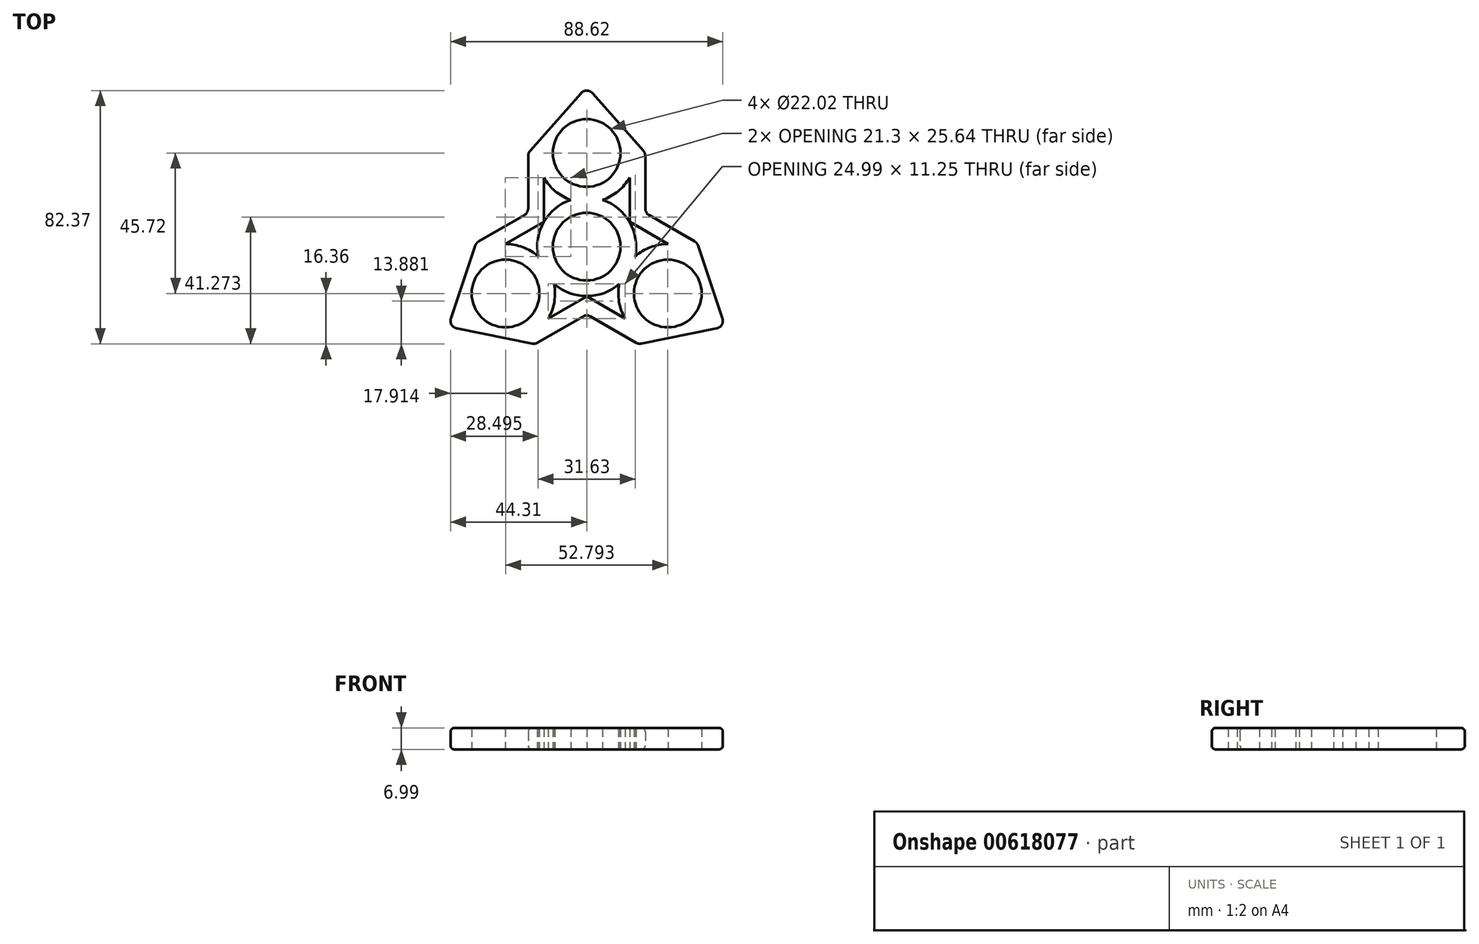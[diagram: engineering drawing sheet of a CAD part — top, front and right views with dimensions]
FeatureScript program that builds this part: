
annotation { "Feature Type Name" : "Feature", "Feature Type Description" : "" }
export const myFeature = defineFeature(function(context is Context, id is Id, definition is map)
    precondition{}
    {
        {
            var Q0;
            Q0=qCreatedBy(makeId("Top.planeOp"),FACE);
            var sketch = newSketch(context, id + "F0", { "sketchPlane" : qUnion([Q0])});
            skCircle(sketch, "E0", {"center": v(0, 0) * mm, "radius": 19.05 * mm});
            skLineSegment(sketch, "E1", {"start": v(0, 0) * mm, "end": v(0, 30.48) * mm});
            skCircle(sketch, "E2", {"center": v(0, 0) * mm, "radius": 11.01 * mm});
            skCircle(sketch, "E3", {"center": v(0, 30.48) * mm, "radius": 11.01 * mm});
            skLineSegment(sketch, "E4", {"start": v(-19.05, 30.48) * mm, "end": v(19.05, 30.48) * mm});
            skLineSegment(sketch, "E5", {"start": v(-19.05, 30.48) * mm, "end": v(0, 52.07) * mm});
            skLineSegment(sketch, "E6", {"start": v(0, 52.07) * mm, "end": v(19.05, 30.48) * mm});
            skLineSegment(sketch, "E7", {"start": v(-19.05, 30.48) * mm, "end": v(-19.05, 0) * mm});
            skLineSegment(sketch, "E8", {"start": v(19.05, 30.48) * mm, "end": v(19.05, 0) * mm});
            skLineSegment(sketch, "E9.1.0", {"start": v(0, 0) * mm, "end": v(-26.4, -15.24) * mm});
            skLineSegment(sketch, "E9.1.1", {"start": v(-45.1, -26.04) * mm, "end": v(-35.92, 1.26) * mm});
            skLineSegment(sketch, "E9.1.2", {"start": v(-16.87, -31.74) * mm, "end": v(9.53, -16.5) * mm});
            skLineSegment(sketch, "E9.1.3", {"start": v(-16.87, -31.74) * mm, "end": v(-45.1, -26.04) * mm});
            skLineSegment(sketch, "E9.1.4", {"start": v(-35.92, 1.26) * mm, "end": v(-9.52, 16.5) * mm});
            skCircle(sketch, "E9.1.5", {"center": v(-26.4, -15.24) * mm, "radius": 11.01 * mm});
            skLineSegment(sketch, "E9.1.6", {"start": v(-16.87, -31.74) * mm, "end": v(-35.92, 1.26) * mm});
            skLineSegment(sketch, "E9.2.0", {"start": v(0, 0) * mm, "end": v(26.4, -15.24) * mm});
            skLineSegment(sketch, "E9.2.1", {"start": v(45.1, -26.04) * mm, "end": v(16.87, -31.74) * mm});
            skLineSegment(sketch, "E9.2.2", {"start": v(35.92, 1.26) * mm, "end": v(9.53, 16.5) * mm});
            skLineSegment(sketch, "E9.2.3", {"start": v(35.92, 1.26) * mm, "end": v(45.1, -26.03) * mm});
            skLineSegment(sketch, "E9.2.4", {"start": v(16.87, -31.74) * mm, "end": v(-9.53, -16.5) * mm});
            skCircle(sketch, "E9.2.5", {"center": v(26.4, -15.24) * mm, "radius": 11.01 * mm});
            skLineSegment(sketch, "E9.2.6", {"start": v(35.92, 1.26) * mm, "end": v(16.87, -31.74) * mm});
            skSolve(sketch);
        }
        {
            var Q0;
            {var subQ0=sQuery(id+"F0.wireOp",EDGE,"E7");var subQ1=sQuery(id+"F0.wireOp",EDGE,"E0");var subQ2=makeQuery(id+"F0.imprint","INTERSECT",VERTEX,{"derivedFrom":[subQ1,subQ0]});Q0=makeQuery(id+"F0.imprint","IMPRINT",FACE,{"disambiguationData":[TD([[makeQuery(id+"F0.imprint","IMPRINT",EDGE,{"disambiguationData":[TD([[subQ2,1.0]])],"derivedFrom":subQ1}),-1.0]])]});}
            var Q1;
            {var subQ0=sQuery(id+"F0.wireOp",EDGE,"E9.1.2");var subQ1=sQuery(id+"F0.wireOp",EDGE,"E0");var subQ2=makeQuery(id+"F0.imprint","INTERSECT",VERTEX,{"derivedFrom":[subQ1,subQ0]});Q1=makeQuery(id+"F0.imprint","IMPRINT",FACE,{"disambiguationData":[TD([[makeQuery(id+"F0.imprint","IMPRINT",EDGE,{"disambiguationData":[TD([[subQ2,1.0]])],"derivedFrom":subQ1}),-1.0]])]});}
            var Q2;
            {var subQ0=sQuery(id+"F0.wireOp",EDGE,"E5");Q2=makeQuery(id+"F0.imprint","IMPRINT",FACE,{"disambiguationData":[TD([[makeQuery(id+"F0.imprint","IMPRINT",EDGE,{"derivedFrom":subQ0}),-1.0]])]});}
            var Q3;
            {var subQ5=sQuery(id+"F0.wireOp",EDGE,"E9.1.1");Q3=makeQuery(id+"F0.imprint","IMPRINT",FACE,{"disambiguationData":[TD([[makeQuery(id+"F0.imprint","IMPRINT",EDGE,{"derivedFrom":subQ5}),-1.0]])]});}
            var Q4;
            {var subQ5=sQuery(id+"F0.wireOp",EDGE,"E9.2.1");Q4=makeQuery(id+"F0.imprint","IMPRINT",FACE,{"disambiguationData":[TD([[makeQuery(id+"F0.imprint","IMPRINT",EDGE,{"derivedFrom":subQ5}),-1.0]])]});}
            var Q5;
            {var subQ3=sQuery(id+"F0.wireOp",EDGE,"E0");var subQ7=sQuery(id+"F0.wireOp",EDGE,"E9.2.2");var subQ9=makeQuery(id+"F0.imprint","INTERSECT",VERTEX,{"derivedFrom":[subQ3,subQ7]});Q5=makeQuery(id+"F0.imprint","IMPRINT",FACE,{"disambiguationData":[TD([[makeQuery(id+"F0.imprint","IMPRINT",EDGE,{"disambiguationData":[TD([[subQ9,1.0]])],"derivedFrom":subQ7}),-1.0]])]});}
            var Q6;
            {var subQ3=sQuery(id+"F0.wireOp",EDGE,"E9.1.4");var subQ5=sQuery(id+"F0.wireOp",EDGE,"E0");var subQ6=makeQuery(id+"F0.imprint","INTERSECT",VERTEX,{"derivedFrom":[subQ5,subQ3]});Q6=makeQuery(id+"F0.imprint","IMPRINT",FACE,{"disambiguationData":[TD([[makeQuery(id+"F0.imprint","IMPRINT",EDGE,{"disambiguationData":[TD([[subQ6,1.0]])],"derivedFrom":subQ3}),1.0]])]});}
            var Q7;
            {var subQ3=sQuery(id+"F0.wireOp",EDGE,"E7");var subQ5=sQuery(id+"F0.wireOp",EDGE,"E0");var subQ6=makeQuery(id+"F0.imprint","INTERSECT",VERTEX,{"derivedFrom":[subQ5,subQ3]});Q7=makeQuery(id+"F0.imprint","IMPRINT",FACE,{"disambiguationData":[TD([[makeQuery(id+"F0.imprint","IMPRINT",EDGE,{"disambiguationData":[TD([[subQ6,1.0]])],"derivedFrom":subQ3}),-1.0]])]});}
            var Q8;
            {var subQ3=sQuery(id+"F0.wireOp",EDGE,"E0");var subQ5=sQuery(id+"F0.wireOp",EDGE,"E9.2.4");var subQ6=makeQuery(id+"F0.imprint","INTERSECT",VERTEX,{"derivedFrom":[subQ3,subQ5]});Q8=makeQuery(id+"F0.imprint","IMPRINT",FACE,{"disambiguationData":[TD([[makeQuery(id+"F0.imprint","IMPRINT",EDGE,{"disambiguationData":[TD([[subQ6,1.0]])],"derivedFrom":subQ5}),1.0]])]});}
            var Q9;
            {var subQ3=sQuery(id+"F0.wireOp",EDGE,"E0");var subQ5=sQuery(id+"F0.wireOp",EDGE,"E9.1.2");var subQ6=makeQuery(id+"F0.imprint","INTERSECT",VERTEX,{"derivedFrom":[subQ3,subQ5]});Q9=makeQuery(id+"F0.imprint","IMPRINT",FACE,{"disambiguationData":[TD([[makeQuery(id+"F0.imprint","IMPRINT",EDGE,{"disambiguationData":[TD([[subQ6,1.0]])],"derivedFrom":subQ5}),-1.0]])]});}
            var Q10;
            {var subQ3=sQuery(id+"F0.wireOp",EDGE,"E0");var subQ5=sQuery(id+"F0.wireOp",EDGE,"E8");var subQ6=makeQuery(id+"F0.imprint","INTERSECT",VERTEX,{"derivedFrom":[subQ3,subQ5]});Q10=makeQuery(id+"F0.imprint","IMPRINT",FACE,{"disambiguationData":[TD([[makeQuery(id+"F0.imprint","IMPRINT",EDGE,{"disambiguationData":[TD([[subQ6,1.0]])],"derivedFrom":subQ5}),1.0]])]});}
            var Q11;
            {var subQ3=sQuery(id+"F0.wireOp",EDGE,"E0");var subQ5=makeQuery(id+"F0.imprint","INTERSECT",VERTEX,{"derivedFrom":[subQ3,sQuery(id+"F0.wireOp",EDGE,"E7")]});Q11=makeQuery(id+"F0.imprint","IMPRINT",FACE,{"disambiguationData":[TD([[makeQuery(id+"F0.imprint","IMPRINT",EDGE,{"disambiguationData":[TD([[subQ5,1.0]])],"derivedFrom":subQ3}),1.0]])]});}
            var Q12;
            {var subQ5=sQuery(id+"F0.wireOp",EDGE,"E0");var subQ6=makeQuery(id+"F0.imprint","INTERSECT",VERTEX,{"derivedFrom":[subQ5,sQuery(id+"F0.wireOp",EDGE,"E9.1.2")]});Q12=makeQuery(id+"F0.imprint","IMPRINT",FACE,{"disambiguationData":[TD([[makeQuery(id+"F0.imprint","IMPRINT",EDGE,{"disambiguationData":[TD([[subQ6,1.0]])],"derivedFrom":subQ5}),1.0]])]});}
            var Q13;
            {var subQ0=sQuery(id+"F0.wireOp",EDGE,"E0");var subQ1=makeQuery(id+"F0.imprint","INTERSECT",VERTEX,{"derivedFrom":[subQ0,sQuery(id+"F0.wireOp",EDGE,"E8")]});Q13=makeQuery(id+"F0.imprint","IMPRINT",FACE,{"disambiguationData":[TD([[makeQuery(id+"F0.imprint","IMPRINT",EDGE,{"disambiguationData":[TD([[subQ1,-1.0]])],"derivedFrom":subQ0}),1.0]])]});}
            var Q14;
            {var subQ0=sQuery(id+"F0.wireOp",EDGE,"E8");var subQ1=sQuery(id+"F0.wireOp",EDGE,"E0");var subQ2=makeQuery(id+"F0.imprint","INTERSECT",VERTEX,{"derivedFrom":[subQ1,subQ0]});Q14=makeQuery(id+"F0.imprint","IMPRINT",FACE,{"disambiguationData":[TD([[makeQuery(id+"F0.imprint","IMPRINT",EDGE,{"disambiguationData":[TD([[subQ2,-1.0]])],"derivedFrom":subQ1}),-1.0]])]});}
            extrude(context, id + "F1", {"entities" : qUnion([Q0, Q1, Q2, Q3, Q4, Q5, Q6, Q7, Q8, Q9, Q10, Q11, Q12, Q13, Q14]), "depth" : 7 * mm, "offsetDistance" : 25.4 * mm});
        }
        {
            var Q0;
            Q0=makeQuery(id+"F1.opExtrude","CAP_FACE",FACE,{"disambiguationData":[OSD([sQuery(id+"F0.wireOp",EDGE,"E2"),sQuery(id+"F0.wireOp",EDGE,"E3"),sQuery(id+"F0.wireOp",EDGE,"E5"),sQuery(id+"F0.wireOp",EDGE,"E6"),sQuery(id+"F0.wireOp",EDGE,"E7"),sQuery(id+"F0.wireOp",EDGE,"E8"),sQuery(id+"F0.wireOp",EDGE,"E9.1.1"),sQuery(id+"F0.wireOp",EDGE,"E9.1.2"),sQuery(id+"F0.wireOp",EDGE,"E9.1.3"),sQuery(id+"F0.wireOp",EDGE,"E9.1.4"),sQuery(id+"F0.wireOp",EDGE,"E9.1.5"),sQuery(id+"F0.wireOp",EDGE,"E9.2.1"),sQuery(id+"F0.wireOp",EDGE,"E9.2.2"),sQuery(id+"F0.wireOp",EDGE,"E9.2.3"),sQuery(id+"F0.wireOp",EDGE,"E9.2.4"),sQuery(id+"F0.wireOp",EDGE,"E9.2.5")])],"isStart":false});
            var Q1;
            Q1=makeQuery(id+"F1.opExtrude","CAP_FACE",FACE,{"disambiguationData":[OSD([sQuery(id+"F0.wireOp",EDGE,"E2"),sQuery(id+"F0.wireOp",EDGE,"E3"),sQuery(id+"F0.wireOp",EDGE,"E5"),sQuery(id+"F0.wireOp",EDGE,"E6"),sQuery(id+"F0.wireOp",EDGE,"E7"),sQuery(id+"F0.wireOp",EDGE,"E8"),sQuery(id+"F0.wireOp",EDGE,"E9.1.1"),sQuery(id+"F0.wireOp",EDGE,"E9.1.2"),sQuery(id+"F0.wireOp",EDGE,"E9.1.3"),sQuery(id+"F0.wireOp",EDGE,"E9.1.4"),sQuery(id+"F0.wireOp",EDGE,"E9.1.5"),sQuery(id+"F0.wireOp",EDGE,"E9.2.1"),sQuery(id+"F0.wireOp",EDGE,"E9.2.2"),sQuery(id+"F0.wireOp",EDGE,"E9.2.3"),sQuery(id+"F0.wireOp",EDGE,"E9.2.4"),sQuery(id+"F0.wireOp",EDGE,"E9.2.5")])],"isStart":true});
            shell(context, id + "F2", {"entities" : qUnion([Q0, Q1]), "thickness" : 5.08 * mm});
        }
        {
            var Q0;
            Q0=makeQuery(id+"F1.opExtrude","SWEPT_EDGE",EDGE,{"disambiguationData":[OSD([sQuery(id+"F0.wireOp",EDGE,"E4"),sQuery(id+"F0.wireOp",EDGE,"E5"),sQuery(id+"F0.wireOp",EDGE,"E7")])]});
            var Q1;
            Q1=makeQuery(id+"F1.opExtrude","SWEPT_EDGE",EDGE,{"disambiguationData":[OSD([sQuery(id+"F0.wireOp",EDGE,"E5"),sQuery(id+"F0.wireOp",EDGE,"E6")])]});
            var Q2;
            Q2=makeQuery(id+"F1.opExtrude","SWEPT_EDGE",EDGE,{"disambiguationData":[OSD([sQuery(id+"F0.wireOp",EDGE,"E7"),sQuery(id+"F0.wireOp",EDGE,"E9.1.4")])]});
            var Q3;
            Q3=makeQuery(id+"F1.opExtrude","SWEPT_EDGE",EDGE,{"disambiguationData":[OSD([sQuery(id+"F0.wireOp",EDGE,"E9.1.1"),sQuery(id+"F0.wireOp",EDGE,"E9.1.4"),sQuery(id+"F0.wireOp",EDGE,"E9.1.6")])]});
            var Q4;
            Q4=makeQuery(id+"F1.opExtrude","SWEPT_EDGE",EDGE,{"disambiguationData":[OSD([sQuery(id+"F0.wireOp",EDGE,"E9.1.1"),sQuery(id+"F0.wireOp",EDGE,"E9.1.3")])]});
            var Q5;
            Q5=makeQuery(id+"F1.opExtrude","SWEPT_EDGE",EDGE,{"disambiguationData":[OSD([sQuery(id+"F0.wireOp",EDGE,"E4"),sQuery(id+"F0.wireOp",EDGE,"E6"),sQuery(id+"F0.wireOp",EDGE,"E8")])]});
            var Q6;
            Q6=makeQuery(id+"F1.opExtrude","SWEPT_EDGE",EDGE,{"disambiguationData":[OSD([sQuery(id+"F0.wireOp",EDGE,"E8"),sQuery(id+"F0.wireOp",EDGE,"E9.2.2")])]});
            var Q7;
            Q7=makeQuery(id+"F1.opExtrude","SWEPT_EDGE",EDGE,{"disambiguationData":[OSD([sQuery(id+"F0.wireOp",EDGE,"E9.2.2"),sQuery(id+"F0.wireOp",EDGE,"E9.2.3"),sQuery(id+"F0.wireOp",EDGE,"E9.2.6")])]});
            var Q8;
            Q8=makeQuery(id+"F1.opExtrude","SWEPT_EDGE",EDGE,{"disambiguationData":[OSD([sQuery(id+"F0.wireOp",EDGE,"E9.2.1"),sQuery(id+"F0.wireOp",EDGE,"E9.2.3")])]});
            var Q9;
            Q9=makeQuery(id+"F1.opExtrude","SWEPT_EDGE",EDGE,{"disambiguationData":[OSD([sQuery(id+"F0.wireOp",EDGE,"E9.2.1"),sQuery(id+"F0.wireOp",EDGE,"E9.2.4"),sQuery(id+"F0.wireOp",EDGE,"E9.2.6")])]});
            var Q10;
            Q10=makeQuery(id+"F1.opExtrude","SWEPT_EDGE",EDGE,{"disambiguationData":[OSD([sQuery(id+"F0.wireOp",EDGE,"E9.1.2"),sQuery(id+"F0.wireOp",EDGE,"E9.2.4")])]});
            var Q11;
            Q11=makeQuery(id+"F1.opExtrude","SWEPT_EDGE",EDGE,{"disambiguationData":[OSD([sQuery(id+"F0.wireOp",EDGE,"E9.1.2"),sQuery(id+"F0.wireOp",EDGE,"E9.1.3"),sQuery(id+"F0.wireOp",EDGE,"E9.1.6")])]});
            fillet(context, id + "F3", {"entities" : qUnion([Q0, Q1, Q2, Q3, Q4, Q5, Q6, Q7, Q8, Q9, Q10, Q11]), "radius" : 2.54 * mm, "tangentPropagation" : true, "allowEdgeOverflow" : false});
        }
        {
            var Q0;
            Q0=makeQuery(id+"F1.opExtrude","CAP_EDGE",EDGE,{"disambiguationData":[OSD([sQuery(id+"F0.wireOp",EDGE,"E9.1.3")])],"isStart":false});
            fillet(context, id + "F4", {"entities" : qUnion([Q0]), "radius" : 1.27 * mm, "tangentPropagation" : true, "allowEdgeOverflow" : false});
        }
        {
            var Q0;
            Q0=makeQuery(id+"F1.opExtrude","CAP_EDGE",EDGE,{"disambiguationData":[OSD([sQuery(id+"F0.wireOp",EDGE,"E6")])],"isStart":true});
            fillet(context, id + "F5", {"entities" : qUnion([Q0]), "radius" : 1.27 * mm, "tangentPropagation" : true, "allowEdgeOverflow" : false});
        }
    });
